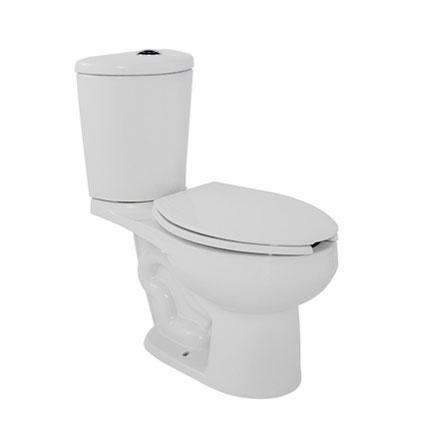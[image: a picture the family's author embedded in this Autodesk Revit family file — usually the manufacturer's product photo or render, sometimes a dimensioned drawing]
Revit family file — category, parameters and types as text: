
# Revit family: WC OPTION_RFA
name_source: partatom
category: Aparatos sanitarios
units: mm (PartAtom-declared; Revit-internal decimal feet)

## family parameters
Compartido = No
Corte con vacíos al cargar = No
Cota de conector redondo = Diámetro de uso
Número OmniClass = 23.45.00.00
Punto de cálculo de habitación = No
Se basa en plano de trabajo = No
Siempre vertical = Sí
Tipo de pieza = Normal
Título OmniClass = Sanitary, Laundry, and Cleaning Equipment

## types (2) — shared parameters
Comentarios de tipo = Ceramic
Compliance = NOM-009-CONAGUA-2001
Elevación por defecto = 0"
Fabricante = HELVEX
Features = Sleek Ergonomic Design; Maximum Efficiency; Flat Base; Sturdy Built; Premium Quality High Gloss (A); Exposed Glazed Trapway; Siphon Action Jetted Bowl; Optimum Water Surface; Certified Intake And Flushing Valves; Silent Intake Valve; Sealed Flushing Valve; Flush Valve With Seal; Setting Kit Included; 5-Yr Warranty In Iron Fittings; Saves On Water Consumption; Less Than 1 gpf Consumption
High Gloss Ceramic = High Gloss Ceramic
Inlet Threads = Feeding: Ø15/16" - 14 NS - 1;  Flush: Couple With Sanitary Flange
Max. Working Pressure = 85.3 psi
Min. Working Pressure = 3.5 psi
Total Width = 15"

## per-type parameters (varying)
| type | Certification | Data Sheet | Descripción | Imagen de tipo | Instructive | Maximum Consumption | Total Height | Total Length | URL |
| TTR | http://helvex.com | http://helvex.com | 1 gpf Olimpia Discharge Spaces Reduced Ecological With Exposed Trapway | <Ninguno> | http://helvex.com | 1.00 gpf | 30" | 26" | http://helvex.com |
| WC OPTION | https://www.helvex.com.mx | https://www.helvex.com.mx | WC TAZA Y TANQUE OPTION, TRAMPA EXPUESTA, ELONGADO, PARA ESPACIOS REDUCIDOS, SIN ASIENTO | WC OPTION.jpg | https://www.helvex.com.mx | 1.20 gpf | 32" | 27" | https://www.helvex.com.mx |

note: column(s) folded — value = type name in every type: Modelo

## geometry (parser evidence)
native form markers: Sweep x2
no freeform markers — native parametric forms only
